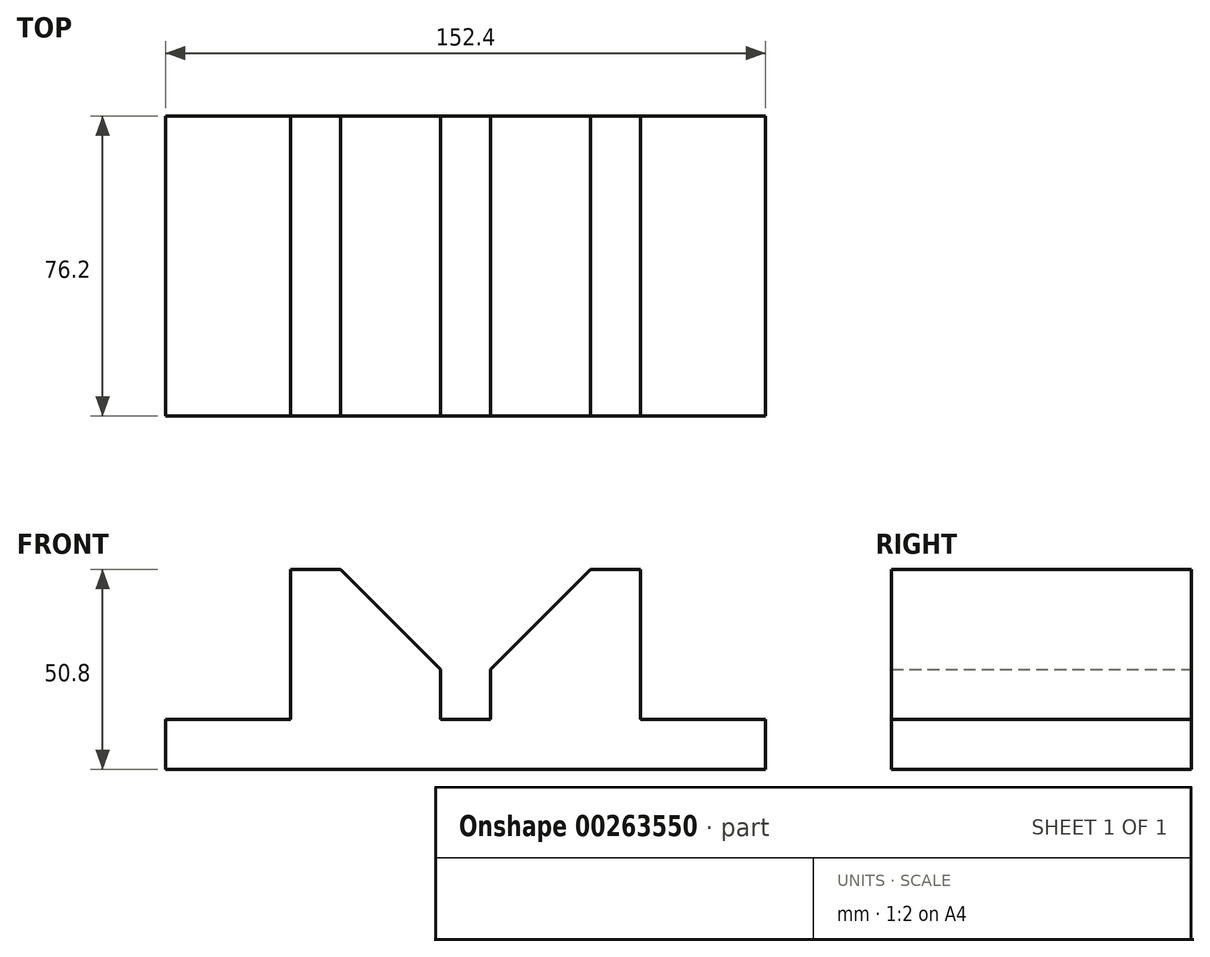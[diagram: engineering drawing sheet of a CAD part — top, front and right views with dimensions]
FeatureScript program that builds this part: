
annotation { "Feature Type Name" : "Feature", "Feature Type Description" : "" }
export const myFeature = defineFeature(function(context is Context, id is Id, definition is map)
    precondition{}
    {
        {
            var Q0;
            Q0=qCreatedBy(makeId("Front.planeOp"),FACE);
            var sketch = newSketch(context, id + "F0", { "sketchPlane" : qUnion([Q0])});
            skLineSegment(sketch, "E0", {"start": v(-62.45, -10.61) * mm, "end": v(-62.45, -23.31) * mm});
            skLineSegment(sketch, "E1", {"start": v(-62.45, -23.31) * mm, "end": v(89.95, -23.31) * mm});
            skLineSegment(sketch, "E2", {"start": v(89.95, -23.31) * mm, "end": v(89.95, -10.61) * mm});
            skLineSegment(sketch, "E3", {"start": v(89.95, -10.61) * mm, "end": v(58.2, -10.61) * mm});
            skLineSegment(sketch, "E4", {"start": v(58.2, -10.61) * mm, "end": v(58.2, 27.49) * mm});
            skLineSegment(sketch, "E5", {"start": v(-62.45, -10.61) * mm, "end": v(-30.7, -10.61) * mm});
            skLineSegment(sketch, "E6", {"start": v(-30.7, -10.61) * mm, "end": v(-30.7, 27.49) * mm});
            skLineSegment(sketch, "E7", {"start": v(7.4, -10.61) * mm, "end": v(7.4, 2.09) * mm});
            skLineSegment(sketch, "E8", {"start": v(20.1, -10.61) * mm, "end": v(20.1, 2.09) * mm});
            skLineSegment(sketch, "E9", {"start": v(-30.7, 27.49) * mm, "end": v(-18, 27.49) * mm});
            skLineSegment(sketch, "E10", {"start": v(58.2, 27.49) * mm, "end": v(45.5, 27.49) * mm});
            skLineSegment(sketch, "E11", {"start": v(20.1, 2.09) * mm, "end": v(45.5, 27.49) * mm});
            skLineSegment(sketch, "E12", {"start": v(-18, 27.49) * mm, "end": v(7.4, 2.09) * mm});
            skLineSegment(sketch, "E13", {"start": v(7.4, -10.61) * mm, "end": v(20.1, -10.61) * mm});
            skSolve(sketch);
        }
        {
            var Q0;
            Q0=makeQuery(id+"F0.imprint","IMPRINT",FACE,{"disambiguationData":[TD([[makeQuery(id+"F0.imprint","IMPRINT",EDGE,{"derivedFrom":sQuery(id+"F0.wireOp",EDGE,"E0")}),1.0]])]});
            extrude(context, id + "F1", {"entities" : qUnion([Q0]), "depth" : 76.2 * mm});
        }
    });
